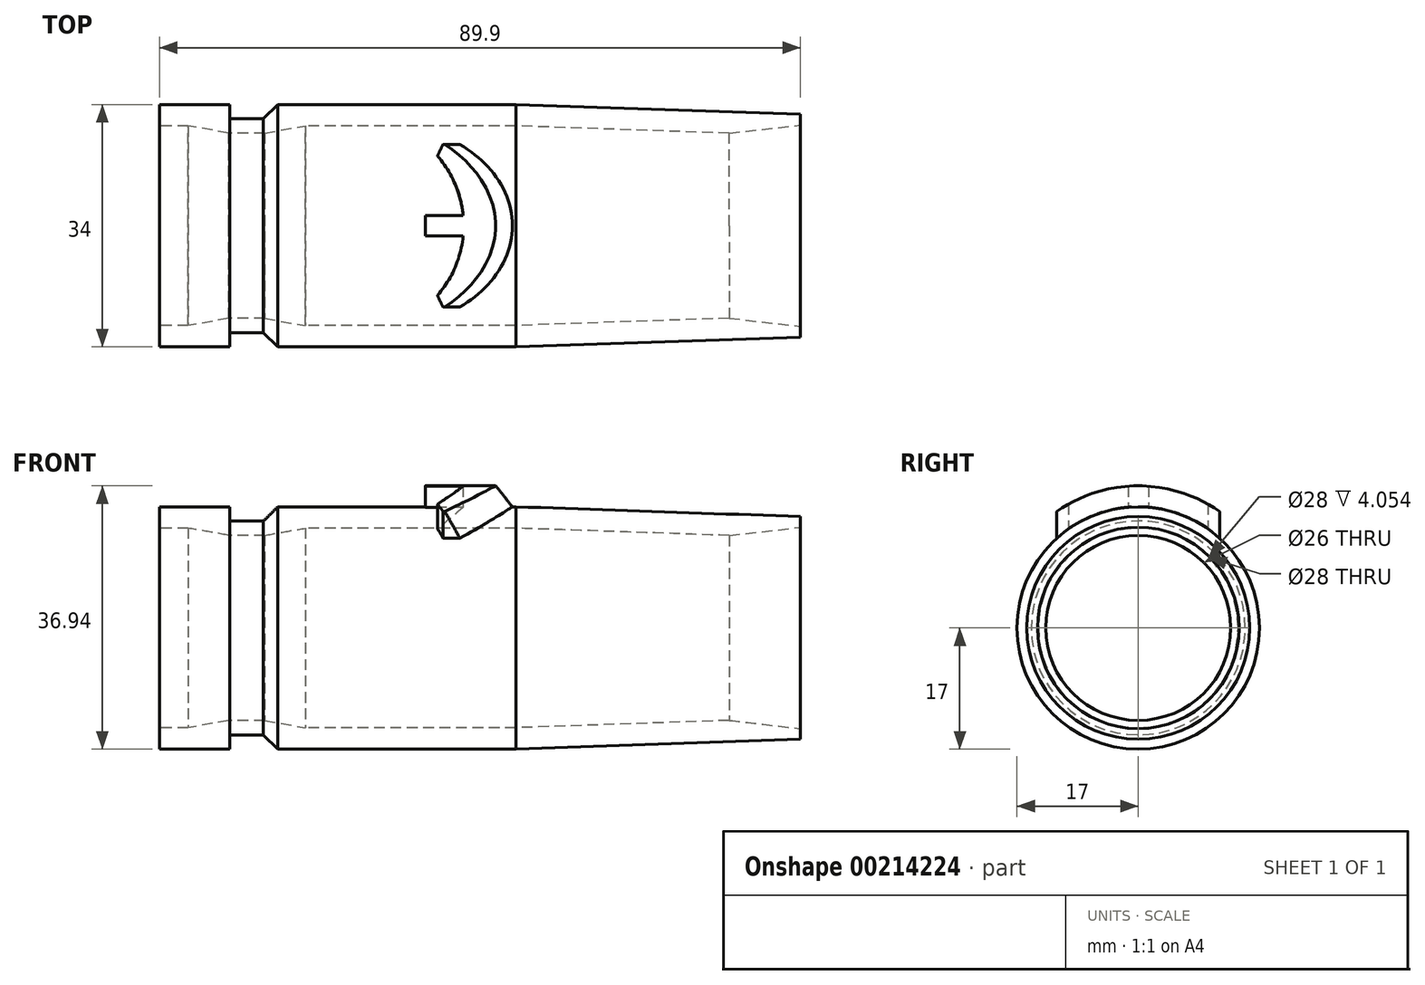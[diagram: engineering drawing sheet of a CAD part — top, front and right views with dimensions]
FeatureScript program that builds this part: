
annotation { "Feature Type Name" : "Feature", "Feature Type Description" : "" }
export const myFeature = defineFeature(function(context is Context, id is Id, definition is map)
    precondition{}
    {
        {
            var Q0;
            Q0=qCreatedBy(makeId("Front.planeOp"),FACE);
            var sketch = newSketch(context, id + "F0", { "sketchPlane" : qUnion([Q0])});
            skLineSegment(sketch, "E0", {"start": v(9.9, -55.88) * mm, "end": v(9.9, 56.52) * mm, "construction": true});
            skLineSegment(sketch, "E1", {"start": v(9.9, 17) * mm, "end": v(9.9, 15) * mm});
            skLineSegment(sketch, "E2", {"start": v(9.9, 15) * mm, "end": v(14.6, 15) * mm});
            skLineSegment(sketch, "E3", {"start": v(14.6, 15) * mm, "end": v(16.6, 17) * mm});
            skLineSegment(sketch, "E4", {"start": v(82.39, 0) * mm, "end": v(-49.14, 0) * mm, "construction": true});
            skLineSegment(sketch, "E5", {"start": v(-18.51, 17) * mm, "end": v(91.63, 17) * mm, "construction": true});
            skLineSegment(sketch, "E6", {"start": v(9.9, 17) * mm, "end": v(0, 17) * mm});
            skLineSegment(sketch, "E7", {"start": v(0, 17) * mm, "end": v(0, 14) * mm});
            skLineSegment(sketch, "E8", {"start": v(16.6, 17) * mm, "end": v(50, 17) * mm});
            skLineSegment(sketch, "E9", {"start": v(89.9, 15.63) * mm, "end": v(50, 17) * mm});
            skLineSegment(sketch, "E10", {"start": v(89.9, 15.63) * mm, "end": v(89.9, 12.63) * mm});
            skLineSegment(sketch, "E11", {"start": v(89.9, 12.63) * mm, "end": v(50, 14) * mm});
            skLineSegment(sketch, "E12", {"start": v(0, 14) * mm, "end": v(4.05, 14) * mm});
            skLineSegment(sketch, "E13", {"start": v(4.05, 14) * mm, "end": v(9.73, 13) * mm});
            skLineSegment(sketch, "E14", {"start": v(9.73, 13) * mm, "end": v(14.77, 13) * mm});
            skLineSegment(sketch, "E15", {"start": v(14.77, 13) * mm, "end": v(20.45, 14) * mm});
            skLineSegment(sketch, "E16", {"start": v(20.45, 14) * mm, "end": v(50, 14) * mm});
            skSolve(sketch);
        }
        {
            var Q0;
            Q0 = qSketchRegion(id + "F0", true);
            var Q1;
            Q1=sQuery(id+"F0.wireOp",EDGE,"E4");
            revolve(context, id + "F1", {"entities" : qUnion([Q0]), "axis" : qUnion([Q1]), "revolveType" : RevolveType.FULL, "oppositeDirection" : true});
        }
        {
            var Q0;
            Q0=qCreatedBy(makeId("Top.planeOp"),FACE);
            var sketch = newSketch(context, id + "F2", { "sketchPlane" : qUnion([Q0])});
            skPoint(sketch, "E17.0", {"position": v(0, 0) * mm});
            skLineSegment(sketch, "E18", {"start": v(0, 117.17) * mm, "end": v(0, -121.8) * mm, "construction": true});
            skLineSegment(sketch, "E19", {"start": v(-129.2, 0) * mm, "end": v(225.05, 0) * mm, "construction": true});
            skLineSegment(sketch, "E20.bottom", {"start": v(37.3, 1.42) * mm, "end": v(42.6, 1.42) * mm});
            skLineSegment(sketch, "E20.top", {"start": v(37.3, -1.42) * mm, "end": v(42.6, -1.42) * mm});
            skLineSegment(sketch, "E20.left", {"start": v(37.3, 1.42) * mm, "end": v(37.3, -1.42) * mm});
            skArc(sketch, "E21", {"start": v(37.3, -11.42) * mm, "mid": v(40.94, -6.95) * mm, "end": v(42.6, -1.42) * mm});
            skArc(sketch, "E22.trimOffspring", {"start": v(42.6, 1.42) * mm, "mid": v(40.94, 6.95) * mm, "end": v(37.3, 11.42) * mm});
            skLineSegment(sketch, "E23", {"start": v(37.3, 11.42) * mm, "end": v(39.5, 11.42) * mm});
            skLineSegment(sketch, "E24", {"start": v(37.3, -11.42) * mm, "end": v(39.5, -11.42) * mm});
            skArc(sketch, "E25", {"start": v(39.5, -11.42) * mm, "mid": v(44.8, 0) * mm, "end": v(39.5, 11.42) * mm});
            skSolve(sketch);
        }
        {
            var Q0;
            Q0 = qSketchRegion(id + "F2", true);
            extrude(context, id + "F3", {"entities" : qUnion([Q0]), "operationType" : NewBodyOperationType.ADD, "depth" : 19.94 * mm});
        }
        {
            var Q0;
            Q0=qCreatedBy(makeId("Right.planeOp"),FACE);
            var sketch = newSketch(context, id + "F4", { "sketchPlane" : qUnion([Q0])});
            skPoint(sketch, "E26.0", {"position": v(0, 0) * mm});
            skCircle(sketch, "E27", {"center": v(0, 0) * mm, "radius": 19.94 * mm});
            skCircle(sketch, "E28", {"center": v(0, 0) * mm, "radius": 24.94 * mm});
            skCircle(sketch, "E29.0", {"center": v(0, 0) * mm, "radius": 17 * mm, "construction": true});
            skSolve(sketch);
        }
        {
            var Q0;
            Q0=makeQuery(id+"F4.imprint","IMPRINT",FACE,{"disambiguationData":[TD([[makeQuery(id+"F4.imprint","IMPRINT",EDGE,{"derivedFrom":sQuery(id+"F4.wireOp",EDGE,"E27")}),-1.0]])]});
            extrude(context, id + "F5", {"entities" : qUnion([Q0]), "operationType" : NewBodyOperationType.REMOVE, "endBound" : BoundingType.THROUGH_ALL, "depth" : 25 * mm});
        }
        {
            var Q0;
            Q0=qCreatedBy(makeId("Right.planeOp"),FACE);
            cPlane(context, id + "F6", {"entities" : qUnion([Q0]), "cplaneType" : CPlaneType.OFFSET, "offset" : 25 * mm, "width" : 150 * mm, "height" : 150 * mm});
        }
        {
            var Q0;
            Q0=qCreatedBy(id+"F6.planeOp",FACE);
            var sketch = newSketch(context, id + "F7", { "sketchPlane" : qUnion([Q0])});
            skPoint(sketch, "E30.0", {"position": v(0, 0) * mm});
            skCircle(sketch, "E31", {"center": v(0, 0) * mm, "radius": 14 * mm});
            skSolve(sketch);
        }
        {
            var Q0;
            Q0 = qSketchRegion(id + "F7", true);
            extrude(context, id + "F8", {"entities" : qUnion([Q0]), "operationType" : NewBodyOperationType.REMOVE, "depth" : 22 * mm});
        }
        {
            var Q0;
            Q0=makeQuery(id+"F1.opRevolve","SWEPT_EDGE",EDGE,{"disambiguationData":[OSD([sQuery(id+"F0.wireOp",EDGE,"E10"),sQuery(id+"F0.wireOp",EDGE,"E11")])]});
            chamfer(context, id + "F9", {"entities" : qUnion([Q0]), "chamferType" : ChamferType.TWO_OFFSETS, "width1" : 1.5 * mm, "oppositeDirection" : false, "width2" : 10 * mm, "tangentPropagation" : true});
        }
        {
            var Q0;
            Q0=makeQuery(id+"F3.boolean.opBoolean","INTERSECT",EDGE,{"derivedFrom":[makeQuery(id+"F1.opRevolve","SWEPT_FACE",FACE,{"disambiguationData":[OSD([sQuery(id+"F0.wireOp",EDGE,"E8")])]}),makeQuery(id+"F3.opExtrude","SWEPT_FACE",FACE,{"disambiguationData":[OSD([sQuery(id+"F2.wireOp",EDGE,"E25")])]})]});
            chamfer(context, id + "F10", {"entities" : qUnion([Q0]), "chamferType" : ChamferType.TWO_OFFSETS, "width1" : 2 * mm, "oppositeDirection" : false, "width2" : 4 * mm, "tangentPropagation" : true});
        }
        {
            var Q0;
            {var subQ0=sQuery(id+"F2.wireOp",EDGE,"E21");var subQ1=sQuery(id+"F2.wireOp",EDGE,"E24");Q0=makeQuery(id+"F3.boolean.opBoolean","SPLIT",EDGE,{"disambiguationData":[TD([makeQuery(id+"F1.opRevolve","SWEPT_FACE",FACE,{"disambiguationData":[OSD([sQuery(id+"F0.wireOp",EDGE,"E8")])]})])],"derivedFrom":makeQuery(id+"F3.opExtrude","SWEPT_EDGE",EDGE,{"disambiguationData":[OSD([subQ0,subQ1])]})});}
            var Q1;
            {var subQ0=sQuery(id+"F2.wireOp",EDGE,"E22.trimOffspring");var subQ1=sQuery(id+"F2.wireOp",EDGE,"E23");Q1=makeQuery(id+"F3.boolean.opBoolean","SPLIT",EDGE,{"disambiguationData":[TD([makeQuery(id+"F1.opRevolve","SWEPT_FACE",FACE,{"disambiguationData":[OSD([sQuery(id+"F0.wireOp",EDGE,"E8")])]})])],"derivedFrom":makeQuery(id+"F3.opExtrude","SWEPT_EDGE",EDGE,{"disambiguationData":[OSD([subQ0,subQ1])]})});}
            chamfer(context, id + "F11", {"entities" : qUnion([Q0, Q1]), "width" : 1 * mm, "tangentPropagation" : true});
        }
    });
